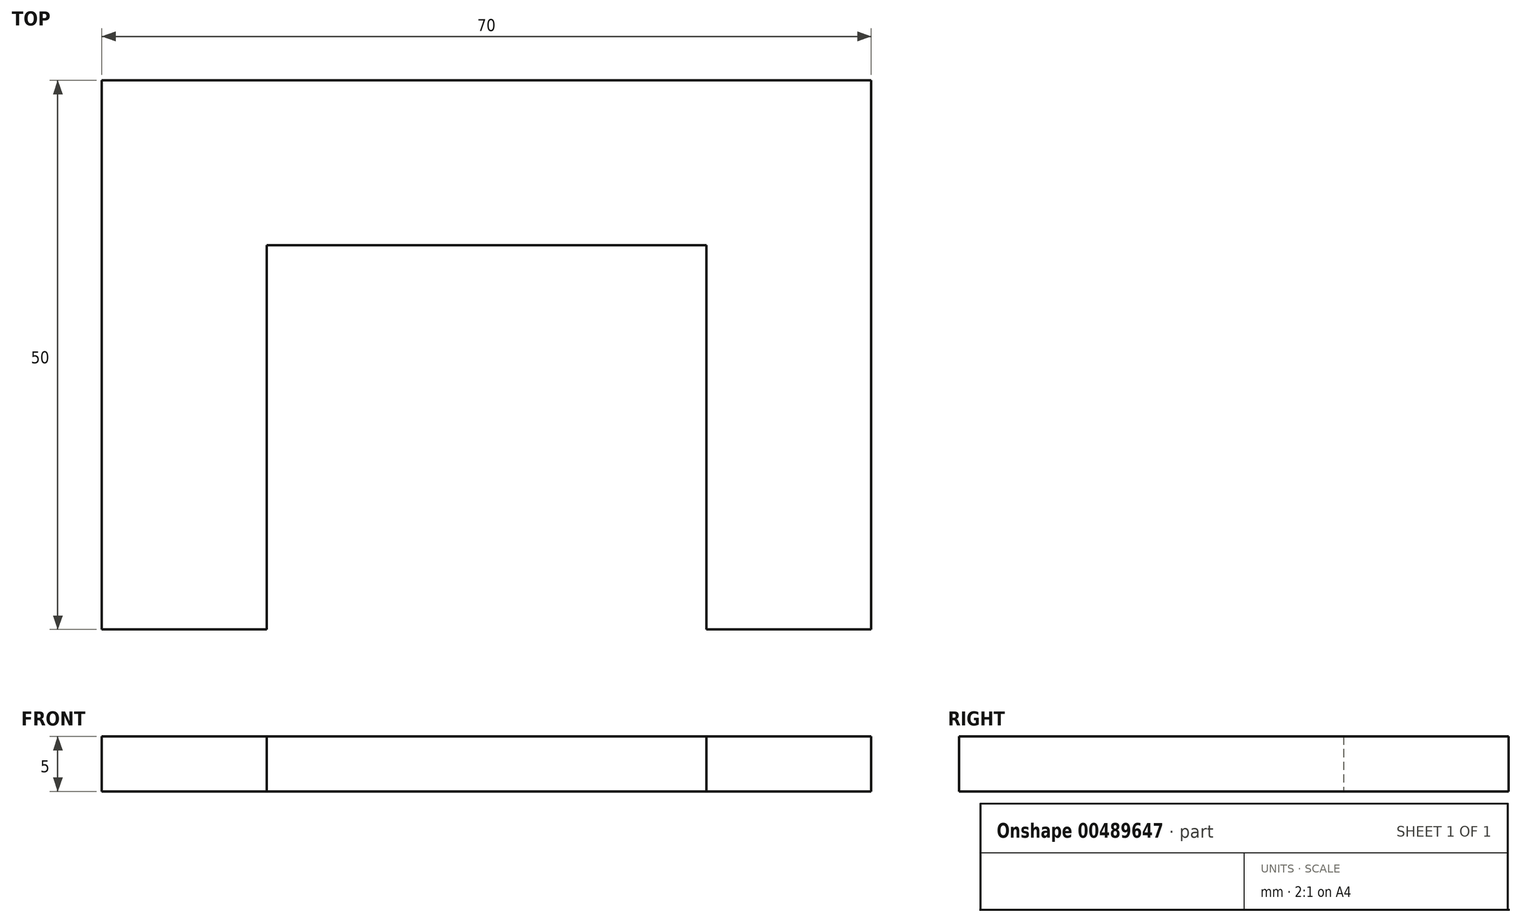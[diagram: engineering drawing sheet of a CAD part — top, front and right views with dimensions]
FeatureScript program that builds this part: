
annotation { "Feature Type Name" : "Feature", "Feature Type Description" : "" }
export const myFeature = defineFeature(function(context is Context, id is Id, definition is map)
    precondition{}
    {
        {
            var Q0;
            Q0=qCreatedBy(makeId("Top.planeOp"),FACE);
            var sketch = newSketch(context, id + "F0", { "sketchPlane" : qUnion([Q0])});
            skLineSegment(sketch, "E0", {"start": v(0, 0) * mm, "end": v(70, 0) * mm});
            skLineSegment(sketch, "E1", {"start": v(70, 0) * mm, "end": v(70, -50) * mm});
            skLineSegment(sketch, "E2", {"start": v(70, -50) * mm, "end": v(55, -50) * mm});
            skLineSegment(sketch, "E3", {"start": v(55, -50) * mm, "end": v(55, -15) * mm});
            skLineSegment(sketch, "E4", {"start": v(0, 0) * mm, "end": v(0, -50) * mm});
            skLineSegment(sketch, "E5", {"start": v(0, -50) * mm, "end": v(15, -50) * mm});
            skLineSegment(sketch, "E6", {"start": v(15, -50) * mm, "end": v(15, -15) * mm});
            skLineSegment(sketch, "E7", {"start": v(15, -15) * mm, "end": v(55, -15) * mm});
            skLineSegment(sketch, "E8", {"start": v(15, -15) * mm, "end": v(15, 0) * mm, "construction": true});
            skSolve(sketch);
        }
        {
            var Q0;
            Q0 = qSketchRegion(id + "F0", true);
            extrude(context, id + "F1", {"entities" : qUnion([Q0]), "depth" : 5 * mm});
        }
    });
